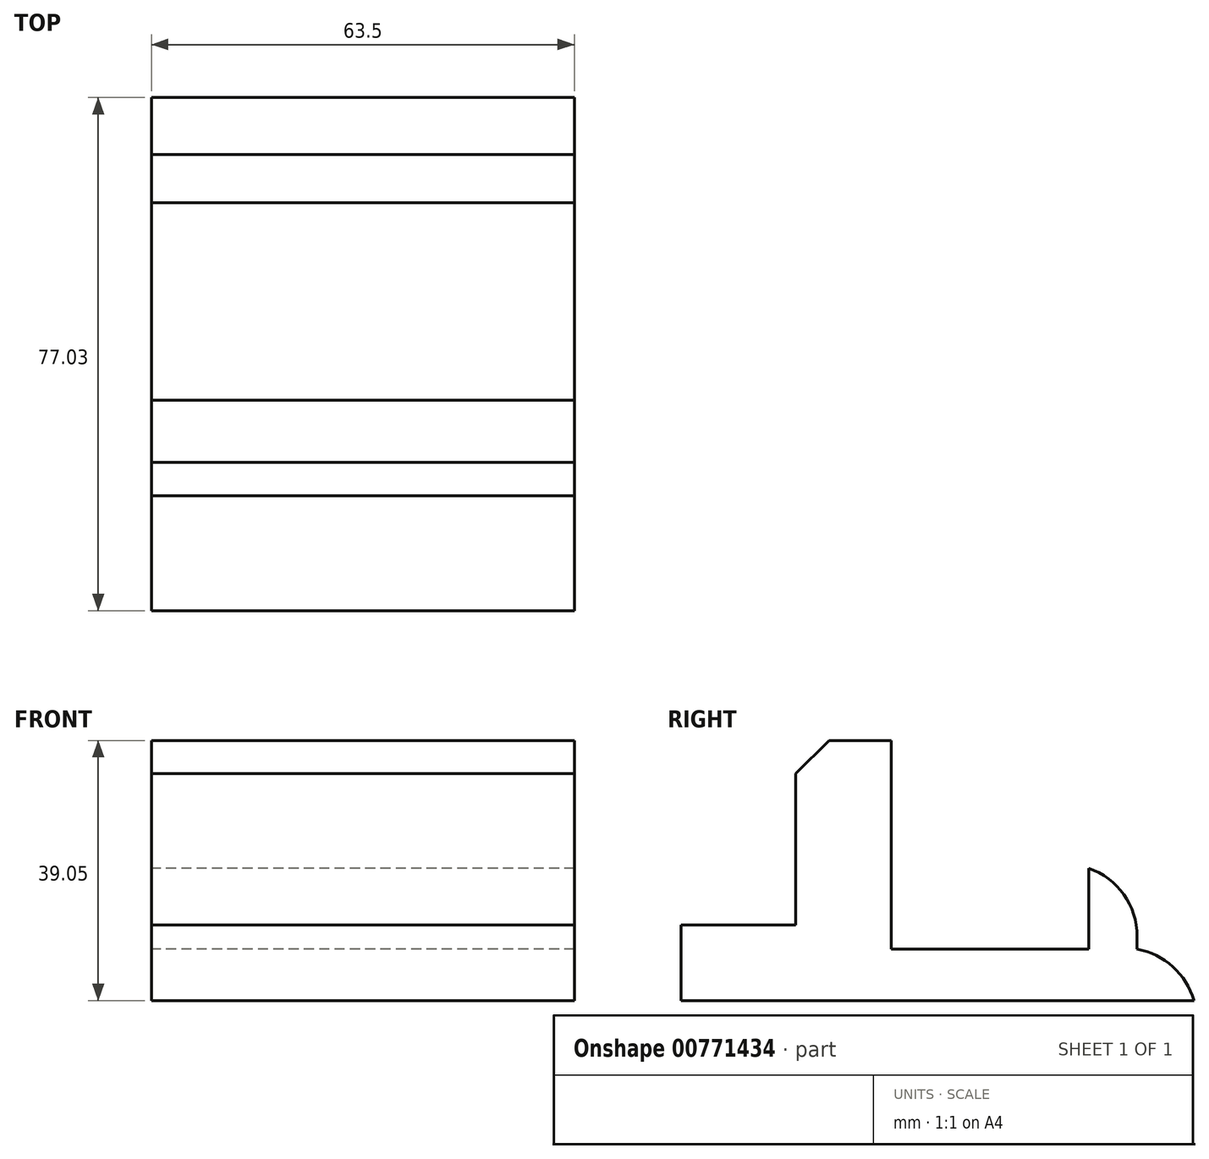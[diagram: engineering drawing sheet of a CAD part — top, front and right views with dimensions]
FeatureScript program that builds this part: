
annotation { "Feature Type Name" : "Feature", "Feature Type Description" : "" }
export const myFeature = defineFeature(function(context is Context, id is Id, definition is map)
    precondition{}
    {
        {
            var Q0;
            Q0=qCreatedBy(makeId("Right.planeOp"),FACE);
            var sketch = newSketch(context, id + "F0", { "sketchPlane" : qUnion([Q0])});
            skLineSegment(sketch, "E0", {"start": v(-43.2, 39.05) * mm, "end": v(-43.2, 0) * mm});
            skLineSegment(sketch, "E1", {"start": v(-43.2, 0) * mm, "end": v(16.99, 0) * mm});
            skLineSegment(sketch, "E2", {"start": v(16.99, 0) * mm, "end": v(16.99, 7.7) * mm});
            skLineSegment(sketch, "E3", {"start": v(16.99, 7.7) * mm, "end": v(8.04, 7.7) * mm});
            skLineSegment(sketch, "E4", {"start": v(8.04, 7.7) * mm, "end": v(8.04, 19.87) * mm});
            skLineSegment(sketch, "E5", {"start": v(8.04, 19.87) * mm, "end": v(0.76, 19.87) * mm});
            skLineSegment(sketch, "E6", {"start": v(0.76, 19.87) * mm, "end": v(0.76, 7.72) * mm});
            skLineSegment(sketch, "E7", {"start": v(0.76, 7.72) * mm, "end": v(-28.89, 7.72) * mm});
            skLineSegment(sketch, "E8", {"start": v(-28.89, 7.72) * mm, "end": v(-28.89, 39.05) * mm});
            skLineSegment(sketch, "E9", {"start": v(-28.89, 39.05) * mm, "end": v(-43.2, 39.05) * mm});
            skLineSegment(sketch, "E10", {"start": v(-43.2, 11.33) * mm, "end": v(-60.46, 11.33) * mm});
            skLineSegment(sketch, "E11", {"start": v(-60.46, 11.33) * mm, "end": v(-60.46, 0) * mm});
            skLineSegment(sketch, "E12", {"start": v(-60.46, 0) * mm, "end": v(-43.2, 0) * mm});
            skSolve(sketch);
        }
        {
            var Q0;
            Q0 = qSketchRegion(id + "F0", true);
            extrude(context, id + "F1", {"entities" : qUnion([Q0]), "depth" : 63.5 * mm, "offsetDistance" : 25 * mm});
        }
        {
            var Q0;
            Q0=makeQuery(id+"F1.opExtrude","SWEPT_EDGE",EDGE,{"disambiguationData":[OSD([sQuery(id+"F0.wireOp",EDGE,"E2"),sQuery(id+"F0.wireOp",EDGE,"E3")])]});
            var Q1;
            Q1=makeQuery(id+"F1.opExtrude","SWEPT_EDGE",EDGE,{"disambiguationData":[OSD([sQuery(id+"F0.wireOp",EDGE,"E4"),sQuery(id+"F0.wireOp",EDGE,"E5")])]});
            fillet(context, id + "F2", {"entities" : qUnion([Q0, Q1]), "radius" : 10.86 * mm, "tangentPropagation" : true, "allowEdgeOverflow" : false});
        }
        {
            var Q0;
            Q0=makeQuery(id+"F1.opExtrude","SWEPT_EDGE",EDGE,{"disambiguationData":[OSD([sQuery(id+"F0.wireOp",EDGE,"E0"),sQuery(id+"F0.wireOp",EDGE,"E9")])]});
            chamfer(context, id + "F3", {"entities" : qUnion([Q0]), "width" : 5 * mm, "tangentPropagation" : true});
        }
    });
